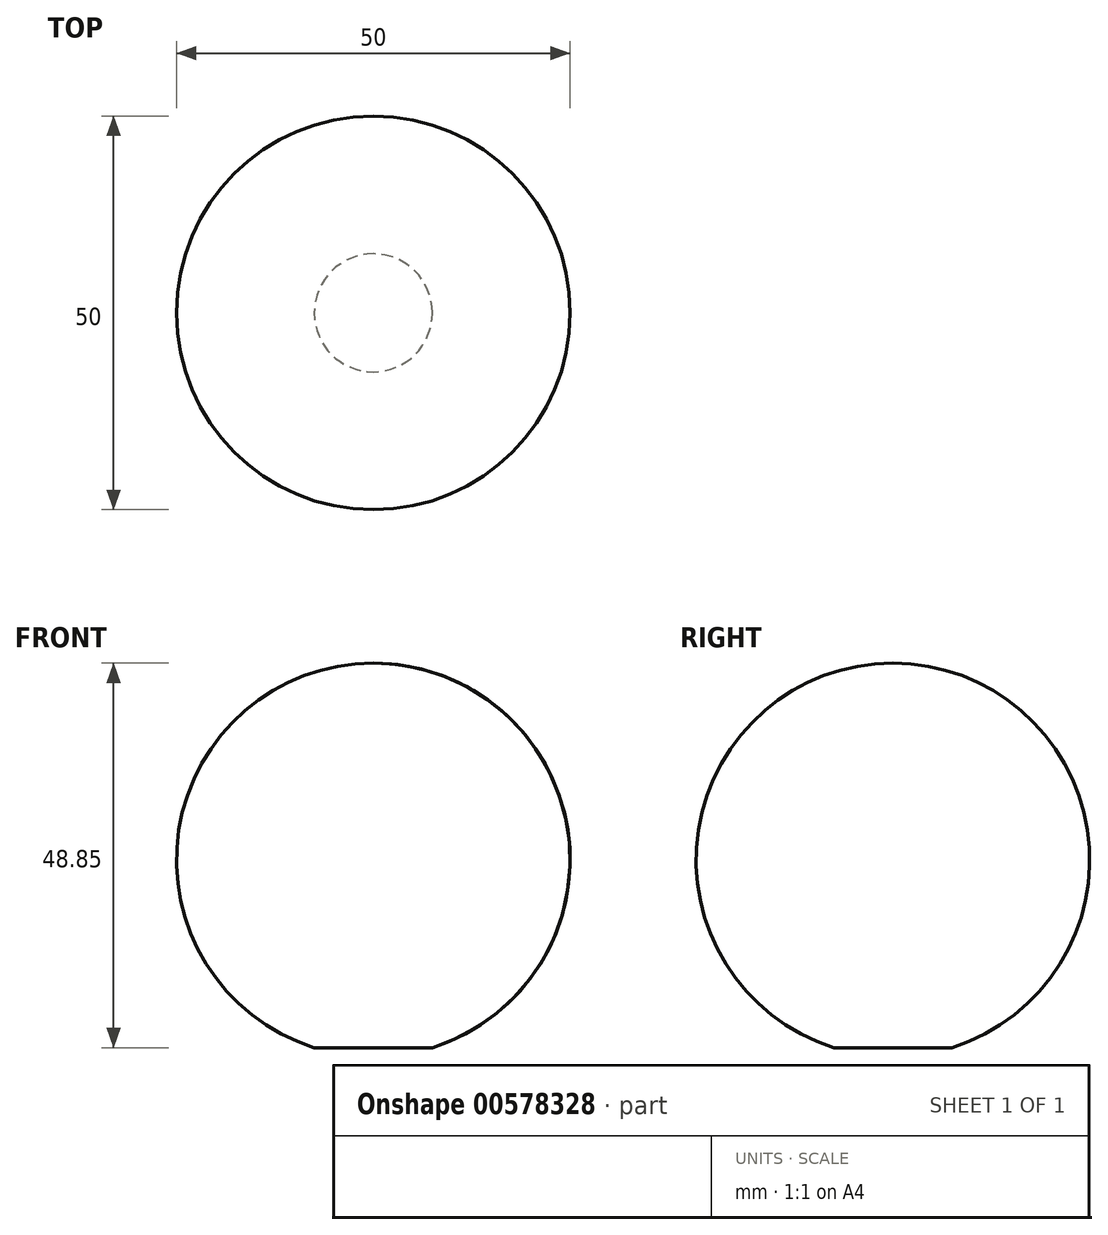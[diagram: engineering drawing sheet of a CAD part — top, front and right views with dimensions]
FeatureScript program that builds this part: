
annotation { "Feature Type Name" : "Feature", "Feature Type Description" : "" }
export const myFeature = defineFeature(function(context is Context, id is Id, definition is map)
    precondition{}
    {
        {
            var Q0;
            Q0=qCreatedBy(makeId("Front.planeOp"),FACE);
            var sketch = newSketch(context, id + "F0", { "sketchPlane" : qUnion([Q0])});
            skArc(sketch, "E0", {"start": v(7.5, -23.85) * mm, "mid": v(24.71, 3.8) * mm, "end": v(0, 25) * mm});
            skLineSegment(sketch, "E1", {"start": v(0, -23.85) * mm, "end": v(7.5, -23.85) * mm});
            skLineSegment(sketch, "E2", {"start": v(0, 25) * mm, "end": v(0, -23.85) * mm, "construction": true});
            skPoint(sketch, "E3.orphan", {"position": v(-7.5, -23.85) * mm});
            skLineSegment(sketch, "E4", {"start": v(0, 25) * mm, "end": v(0, -23.85) * mm});
            skSolve(sketch);
        }
        {
            var Q0;
            Q0=makeQuery(id+"F0.imprint","IMPRINT",FACE,{"disambiguationData":[TD([[makeQuery(id+"F0.imprint","IMPRINT",EDGE,{"derivedFrom":sQuery(id+"F0.wireOp",EDGE,"E0")}),1.0]])]});
            var Q1;
            Q1=sQuery(id+"F0.wireOp",EDGE,"E4");
            revolve(context, id + "F1", {"entities" : qUnion([Q0]), "axis" : qUnion([Q1]), "revolveType" : RevolveType.FULL});
        }
    });
